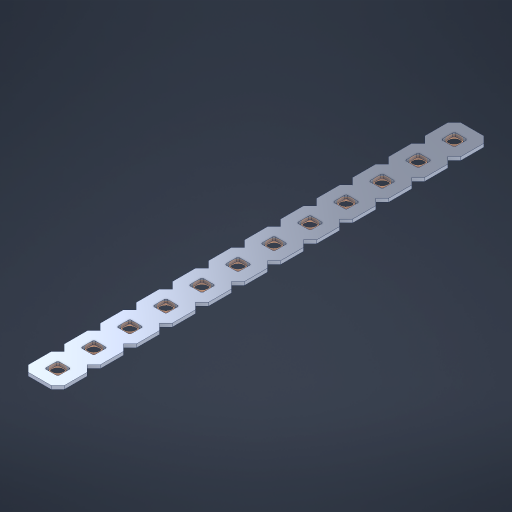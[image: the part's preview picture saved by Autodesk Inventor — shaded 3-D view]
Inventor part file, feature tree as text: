
AUTODESK INVENTOR PART (.ipt)
format: ipt  version: 2023 (Build 270158000, 158)  size: 415,232 bytes
history: native  units: in
note: dims shown in document units (in); Inventor stores cm internally (conversion verified against a paired STEP export)
features: other x13, extrude x11, sketch x2, pattern_linear x1
ambient origin geometry x8: Origin, YZ Plane, XZ Plane, XY Plane, X Axis, Y Axis, Z Axis, Center Point
bodies: Solid1 (feature_tree), Body (feature_tree)
feature tree (27):
  pattern_linear  "Rectangular Pattern1"  Spacing1=0.09in  [1 undecoded]
  sketch  "Sketch1"  dims[d1=0.5in]
  sketch  "Sketch2"  dims[d2=0.182in d3=0.09in d4=0.09in d5=0.09in d6=0.09in d7=0.09in d8=0.09in d9=0.09in d10=0.09in d11=0.02in d13=0.0in d14=0.172in d15=0.0625in d16=0.0in d19=0.5in d22=0.5in]
  other  "Srf1"
  other  "Srf126"
  other  "Srf127"
  other  "Srf128"
  other  "Srf129"
  other  "Srf130"
  other  "Srf131"
  other  "Srf250"
  other  "Srf251"
  other  "Srf252"
  other  "Srf253"
  other  "Srf254"
  other  "Circle"
  extrude  "ExtrusionSrf126"  Depth=0.09in
  extrude  "ExtrusionSrf127"  Depth=0.09in
  extrude  "ExtrusionSrf128"  Depth=0.09in
  extrude  "ExtrusionSrf129"  Depth=0.09in
  extrude  "ExtrusionSrf130"  Depth=0.09in
  extrude  "ExtrusionSrf131"  Depth=0.09in
  extrude  "ExtrusionSrf250"  Depth=0.09in
  extrude  "ExtrusionSrf251"  Depth=0.02in
  extrude  "ExtrusionSrf252"  TaperAngle=0.0deg  [1 undecoded]
  extrude  "ExtrusionSrf253"  Depth=0.5in
  extrude  "ExtrusionSrf254"  Depth=0.5in TaperAngle=0.0deg
note: 2 required parameter values undecoded (feature->parameter linkage not recoverable at this tier; creation-order binding heuristic only, values carry confidence <= 0.55)
